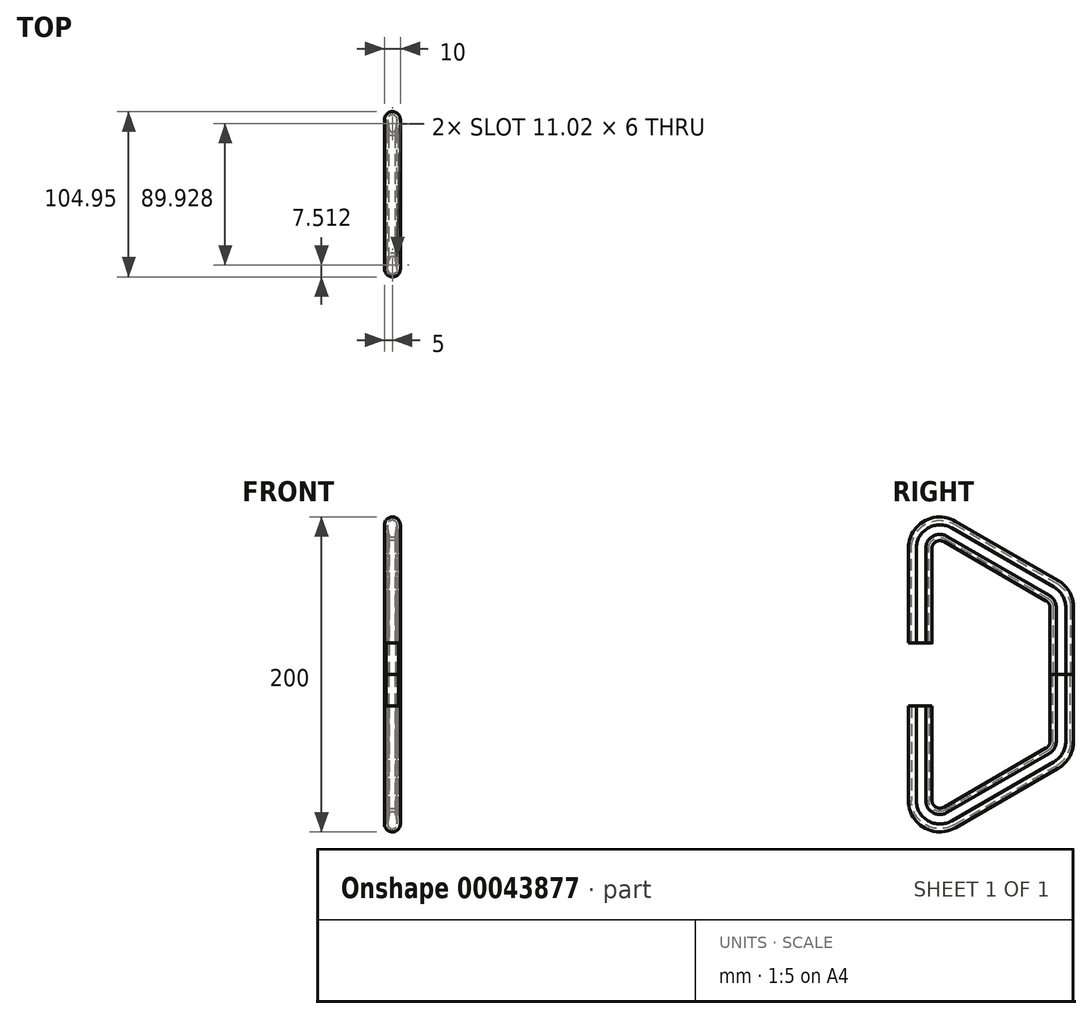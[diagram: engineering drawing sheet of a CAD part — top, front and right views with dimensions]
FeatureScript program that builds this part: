
annotation { "Feature Type Name" : "Feature", "Feature Type Description" : "" }
export const myFeature = defineFeature(function(context is Context, id is Id, definition is map)
    precondition{}
    {
        {
            var Q0;
            Q0=qCreatedBy(makeId("Top.planeOp"),FACE);
            cPlane(context, id + "F0", {"entities" : qUnion([Q0]), "cplaneType" : CPlaneType.OFFSET, "offset" : 20 * mm, "width" : 150 * mm, "height" : 150 * mm});
        }
        {
            var Q0;
            Q0=qCreatedBy(id+"F0.planeOp",FACE);
            var sketch = newSketch(context, id + "F4", { "sketchPlane" : qUnion([Q0])});
            skArc(sketch, "E0", {"start": v(-3, 0) * mm, "mid": v(0, -3) * mm, "end": v(3, 0) * mm});
            skLineSegment(sketch, "E1", {"start": v(-5, 0) * mm, "end": v(-3, 0) * mm});
            skLineSegment(sketch, "E2.trimOffspring", {"start": v(3, 0) * mm, "end": v(5, 0) * mm});
            skArc(sketch, "E3", {"start": v(-5, 0) * mm, "mid": v(0, -5) * mm, "end": v(5, 0) * mm});
            skLineSegment(sketch, "E4", {"start": v(5, 0) * mm, "end": v(4, 6.02) * mm});
            skLineSegment(sketch, "E5.MirrorCS", {"start": v(-5, 0) * mm, "end": v(-4, 6.02) * mm});
            skArc(sketch, "E6", {"start": v(4, 6.02) * mm, "mid": v(0, 10.02) * mm, "end": v(-4, 6.02) * mm});
            skArc(sketch, "E7", {"start": v(2, 6.02) * mm, "mid": v(0, 8.02) * mm, "end": v(-2, 6.02) * mm});
            skLineSegment(sketch, "E8", {"start": v(3, 0) * mm, "end": v(2, 6.02) * mm});
            skLineSegment(sketch, "E9.MirrorCS", {"start": v(-3, 0) * mm, "end": v(-2, 6.02) * mm});
            skSolve(sketch);
        }
        {
            var Q0;
            Q0=qCreatedBy(makeId("Right.planeOp"),FACE);
            var sketch = newSketch(context, id + "F1", { "sketchPlane" : qUnion([Q0])});
            skLineSegment(sketch, "E10", {"start": v(0, 20) * mm, "end": v(0, 80) * mm});
            skLineSegment(sketch, "E11", {"start": v(22.5, 93) * mm, "end": v(87.45, 55.5) * mm});
            skLineSegment(sketch, "E12", {"start": v(94.95, 42.5) * mm, "end": v(94.95, 0) * mm});
            skPoint(sketch, "E13.visualSharp", {"position": v(0, 105.98) * mm});
            skArc(sketch, "E13.filletArc", {"start": v(22.5, 93) * mm, "mid": v(7.5, 93) * mm, "end": v(0, 80) * mm});
            skPoint(sketch, "E14.visualSharp", {"position": v(94.95, 51.16) * mm});
            skArc(sketch, "E14.filletArc", {"start": v(94.95, 42.5) * mm, "mid": v(92.94, 50) * mm, "end": v(87.45, 55.5) * mm});
            skSolve(sketch);
        }
        {
            var Q0;
            Q0 = qSketchRegion(id + "F4", true);
            var Q1;
            Q1 = qConstructionFilter(qBodyType(qCreatedBy(id + "F1" ,EDGE), BodyType.WIRE), ConstructionObject.NO);
            sweep(context, id + "F2", {"profiles" : qUnion([Q0]), "path" : qUnion([Q1])});
        }
        {
            var Q0;
            Q0=makeQuery(id+"F2.opSweep","SWEPT_BODY",BODY,{"disambiguationData":[OSD([sQuery(id+"F4.wireOp",EDGE,"E0"),sQuery(id+"F4.wireOp",EDGE,"E1"),sQuery(id+"F4.wireOp",EDGE,"E2.trimOffspring"),sQuery(id+"F4.wireOp",EDGE,"E3"),sQuery(id+"F1.wireOp",EDGE,"E10")])]});
            var Q1;
            Q1=qCreatedBy(makeId("Top.planeOp"),FACE);
            mirror(context, id + "F3", {"entities" : qUnion([Q0]), "mirrorPlane" : qUnion([Q1])});
        }
    });
